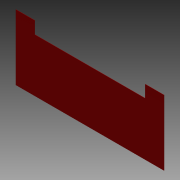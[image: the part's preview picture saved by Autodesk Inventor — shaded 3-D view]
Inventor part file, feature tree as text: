
AUTODESK INVENTOR PART (.ipt)
format: ipt  version: 2013 (Build 170138000, 138)  size: 76,800 bytes
history: native  units: in
note: dims shown in document units (in); Inventor stores cm internally (conversion verified against a paired STEP export)
features: extrude x1, sketch x1
ambient origin geometry x8: Origin, YZ Plane, XZ Plane, XY Plane, X Axis, Y Axis, Z Axis, Center Point
bodies: Solid1 (feature_tree)
feature tree (2):
  extrude  "Extrusion1"  Depth=32.0in
  sketch  "Sketch1"  dims[d0=72.5in d1=32.0in d2=9.25in d3=6.0in d4=9.25in d5=6.0in d6=0.125in d7=0.0in]
